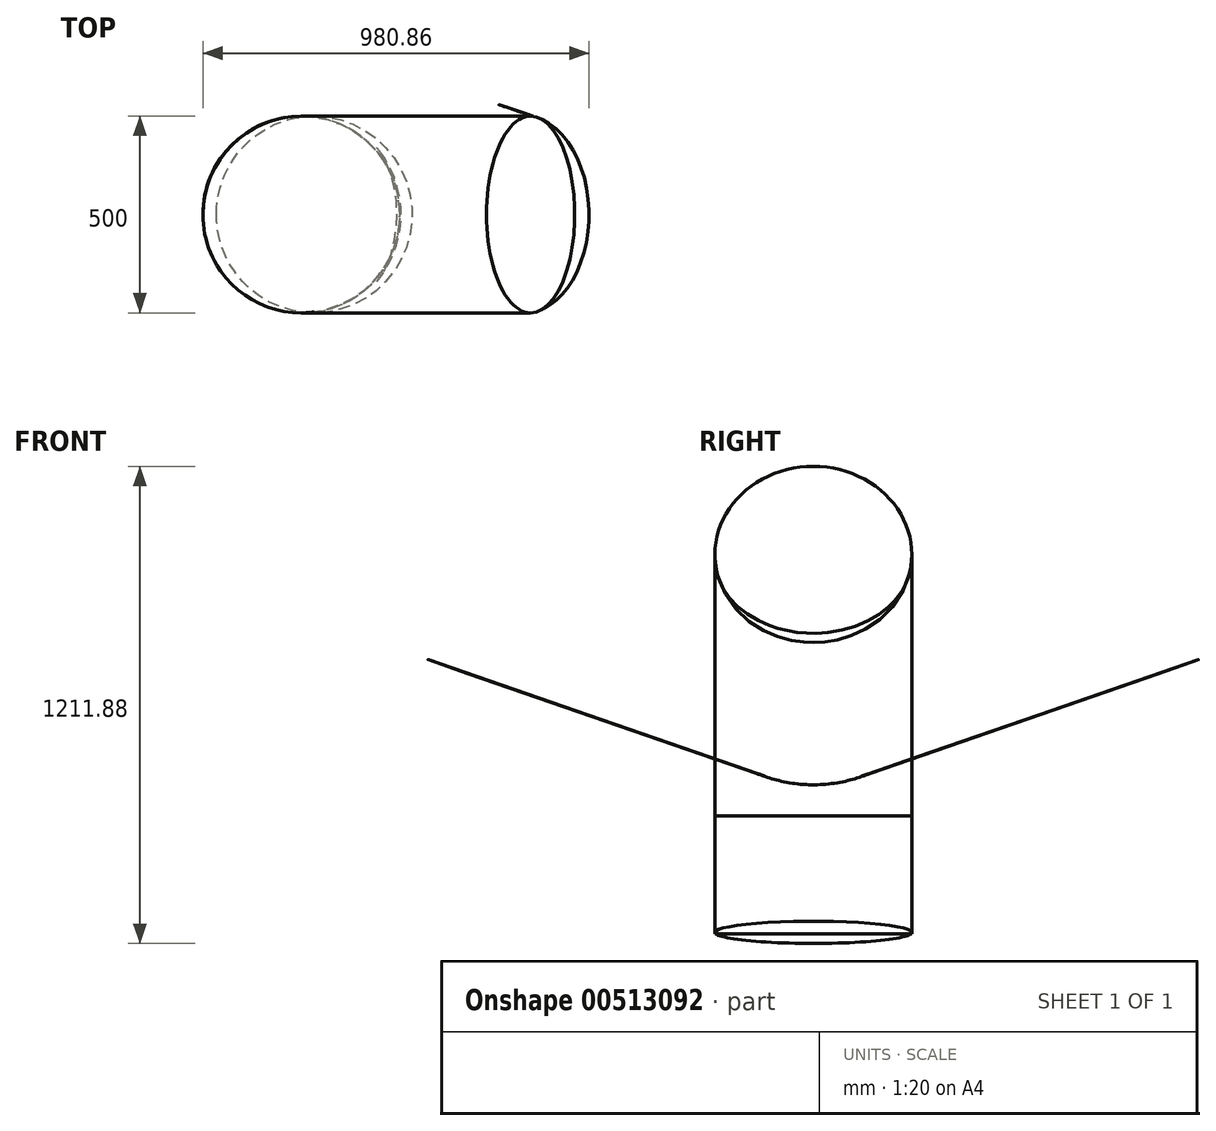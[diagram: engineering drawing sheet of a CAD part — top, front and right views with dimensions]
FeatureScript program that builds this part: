
annotation { "Feature Type Name" : "Feature", "Feature Type Description" : "" }
export const myFeature = defineFeature(function(context is Context, id is Id, definition is map)
    precondition{}
    {
        {
            var Q0;
            Q0=qCreatedBy(makeId("Front.planeOp"),FACE);
            var sketch = newSketch(context, id + "F0", { "sketchPlane" : qUnion([Q0])});
            skLineSegment(sketch, "E0.bottom", {"start": v(0, 0) * mm, "end": v(250, 0) * mm});
            skLineSegment(sketch, "E0.top", {"start": v(0, 300) * mm, "end": v(250, 300) * mm});
            skLineSegment(sketch, "E0.left", {"start": v(0, 0) * mm, "end": v(0, 300) * mm});
            skLineSegment(sketch, "E0.right", {"start": v(250, 0) * mm, "end": v(250, 300) * mm});
            skSolve(sketch);
        }
        {
            var Q0;
            Q0=makeQuery(id+"F0.imprint","IMPRINT",FACE,{"disambiguationData":[TD([[makeQuery(id+"F0.imprint","IMPRINT",EDGE,{"derivedFrom":sQuery(id+"F0.wireOp",EDGE,"E0.bottom")}),1.0]])]});
            var Q1;
            Q1=sQuery(id+"F0.wireOp",EDGE,"E0.top");
            var Q2;
            Q2=sQuery(id+"F0.wireOp",EDGE,"E0.left");
            var Q3;
            Q3=sQuery(id+"F0.wireOp",EDGE,"E0.right");
            var Q4;
            Q4=sQuery(id+"F0.wireOp",EDGE,"E0.bottom");
            var Q5;
            Q5=sQuery(id+"F0.wireOp",EDGE,"E0.left");
            revolve(context, id + "F1", {"entities" : qUnion([Q0]), "surfaceEntities" : qUnion([Q1, Q2, Q3, Q4]), "axis" : qUnion([Q5]), "revolveType" : RevolveType.FULL});
        }
        {
            var Q0;
            Q0=qCreatedBy(makeId("Front.planeOp"),FACE);
            var sketch = newSketch(context, id + "F2", { "sketchPlane" : qUnion([Q0])});
            skFitSpline(sketch, "E1", {"points": [v(0, 0) * mm, v(0, 517.47) * mm, v(220.85, 703.75) * mm, v(458.71, 890.02) * mm, v(550.42, 981.73) * mm, v(567.61, 993.2) * mm], "startDerivative": vector(-276.16, 1923.45) * mm, "endDerivative": vector(240.47, 129.74) * mm});
            skSolve(sketch);
        }
        {
            var Q0;
            Q0=makeQuery(id+"F1.opRevolve","SWEPT_FACE",FACE,{"disambiguationData":[OSD([sQuery(id+"F0.wireOp",EDGE,"E0.top")])]});
            var Q1;
            Q1=sQuery(id+"F2.wireOp",EDGE,"E1");
            sweep(context, id + "F3", {"profiles" : qUnion([Q0]), "path" : qUnion([Q1])});
        }
    });
